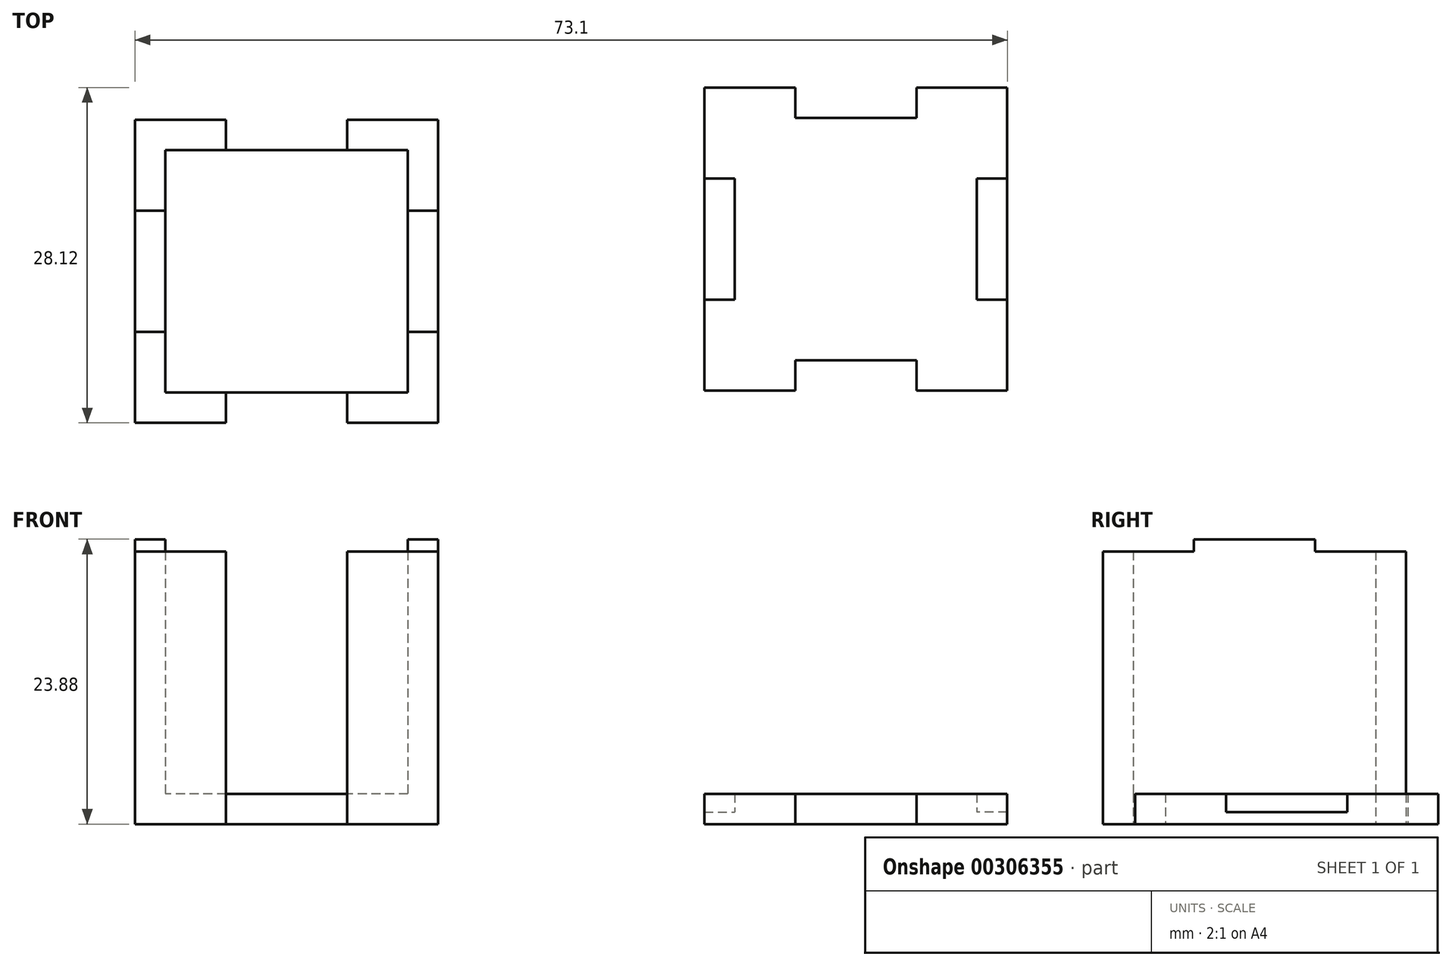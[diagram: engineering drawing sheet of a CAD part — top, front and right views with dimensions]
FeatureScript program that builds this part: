
annotation { "Feature Type Name" : "Feature", "Feature Type Description" : "" }
export const myFeature = defineFeature(function(context is Context, id is Id, definition is map)
    precondition{}
    {
        {
            var Q0;
            Q0=qCreatedBy(makeId("Top.planeOp"),FACE);
            var sketch = newSketch(context, id + "F0", { "sketchPlane" : qUnion([Q0])});
            skLineSegment(sketch, "E0.bottom", {"start": v(12.7, -12.7) * mm, "end": v(-12.7, -12.7) * mm});
            skLineSegment(sketch, "E0.top", {"start": v(12.7, 12.7) * mm, "end": v(-12.7, 12.7) * mm});
            skLineSegment(sketch, "E0.left", {"start": v(12.7, -12.7) * mm, "end": v(12.7, 12.7) * mm});
            skLineSegment(sketch, "E0.right", {"start": v(-12.7, -12.7) * mm, "end": v(-12.7, 12.7) * mm});
            skPoint(sketch, "E0.middle", {"position": v(0, 0) * mm});
            skLineSegment(sketch, "E1.bottom", {"start": v(-5.08, 12.7) * mm, "end": v(5.08, 12.7) * mm});
            skLineSegment(sketch, "E1.top", {"start": v(-5.08, 10.16) * mm, "end": v(5.08, 10.16) * mm});
            skLineSegment(sketch, "E1.left", {"start": v(-5.08, 12.7) * mm, "end": v(-5.08, 10.16) * mm});
            skLineSegment(sketch, "E1.right", {"start": v(5.08, 12.7) * mm, "end": v(5.08, 10.16) * mm});
            skLineSegment(sketch, "E2.bottom", {"start": v(-12.7, 5.08) * mm, "end": v(-10.16, 5.08) * mm});
            skLineSegment(sketch, "E2.top", {"start": v(-12.7, -5.08) * mm, "end": v(-10.16, -5.08) * mm});
            skLineSegment(sketch, "E2.left", {"start": v(-12.7, 5.08) * mm, "end": v(-12.7, -5.08) * mm});
            skLineSegment(sketch, "E2.right", {"start": v(-10.16, 5.08) * mm, "end": v(-10.16, -5.08) * mm});
            skLineSegment(sketch, "E3.bottom", {"start": v(-5.08, -12.7) * mm, "end": v(5.08, -12.7) * mm});
            skLineSegment(sketch, "E3.top", {"start": v(-5.08, -10.16) * mm, "end": v(5.08, -10.16) * mm});
            skLineSegment(sketch, "E3.left", {"start": v(-5.08, -12.7) * mm, "end": v(-5.08, -10.16) * mm});
            skLineSegment(sketch, "E3.right", {"start": v(5.08, -12.7) * mm, "end": v(5.08, -10.16) * mm});
            skLineSegment(sketch, "E4.bottom", {"start": v(12.7, 5.08) * mm, "end": v(10.16, 5.08) * mm});
            skLineSegment(sketch, "E4.top", {"start": v(12.7, -5.08) * mm, "end": v(10.16, -5.08) * mm});
            skLineSegment(sketch, "E4.left", {"start": v(12.7, 5.08) * mm, "end": v(12.7, -5.08) * mm});
            skLineSegment(sketch, "E4.right", {"start": v(10.16, 5.08) * mm, "end": v(10.16, -5.08) * mm});
            skLineSegment(sketch, "E5.bottom", {"start": v(10.16, -10.16) * mm, "end": v(-10.16, -10.16) * mm});
            skLineSegment(sketch, "E5.top", {"start": v(10.16, 10.16) * mm, "end": v(-10.16, 10.16) * mm});
            skLineSegment(sketch, "E5.left", {"start": v(10.16, -10.16) * mm, "end": v(10.16, 10.16) * mm});
            skLineSegment(sketch, "E5.right", {"start": v(-10.16, -10.16) * mm, "end": v(-10.16, 10.16) * mm});
            skLineSegment(sketch, "E6.bottom", {"start": v(60.4, -9.98) * mm, "end": v(35, -9.98) * mm});
            skLineSegment(sketch, "E6.top", {"start": v(60.4, 15.42) * mm, "end": v(35, 15.42) * mm});
            skLineSegment(sketch, "E6.left", {"start": v(60.4, -9.98) * mm, "end": v(60.4, 15.42) * mm});
            skLineSegment(sketch, "E6.right", {"start": v(35, -9.98) * mm, "end": v(35, 15.42) * mm});
            skPoint(sketch, "E6.middle", {"position": v(47.7, 2.72) * mm});
            skLineSegment(sketch, "E7.bottom", {"start": v(42.62, 15.42) * mm, "end": v(52.78, 15.42) * mm});
            skLineSegment(sketch, "E7.top", {"start": v(42.62, 12.88) * mm, "end": v(52.78, 12.88) * mm});
            skLineSegment(sketch, "E7.left", {"start": v(42.62, 15.42) * mm, "end": v(42.62, 12.88) * mm});
            skLineSegment(sketch, "E7.right", {"start": v(52.78, 15.42) * mm, "end": v(52.78, 12.88) * mm});
            skLineSegment(sketch, "E8.bottom", {"start": v(35, 7.8) * mm, "end": v(37.54, 7.8) * mm});
            skLineSegment(sketch, "E8.top", {"start": v(35, -2.36) * mm, "end": v(37.54, -2.36) * mm});
            skLineSegment(sketch, "E8.left", {"start": v(35, 7.8) * mm, "end": v(35, -2.36) * mm});
            skLineSegment(sketch, "E8.right", {"start": v(37.54, 7.8) * mm, "end": v(37.54, -2.36) * mm});
            skLineSegment(sketch, "E9.bottom", {"start": v(42.62, -9.98) * mm, "end": v(52.78, -9.98) * mm});
            skLineSegment(sketch, "E9.top", {"start": v(42.62, -7.44) * mm, "end": v(52.78, -7.44) * mm});
            skLineSegment(sketch, "E9.left", {"start": v(42.62, -9.98) * mm, "end": v(42.62, -7.44) * mm});
            skLineSegment(sketch, "E9.right", {"start": v(52.78, -9.98) * mm, "end": v(52.78, -7.44) * mm});
            skLineSegment(sketch, "E10.bottom", {"start": v(60.4, 7.8) * mm, "end": v(57.86, 7.8) * mm});
            skLineSegment(sketch, "E10.top", {"start": v(60.4, -2.36) * mm, "end": v(57.86, -2.36) * mm});
            skLineSegment(sketch, "E10.left", {"start": v(60.4, 7.8) * mm, "end": v(60.4, -2.36) * mm});
            skLineSegment(sketch, "E10.right", {"start": v(57.86, 7.8) * mm, "end": v(57.86, -2.36) * mm});
            skLineSegment(sketch, "E11.bottom", {"start": v(57.86, -7.44) * mm, "end": v(37.54, -7.44) * mm});
            skLineSegment(sketch, "E11.top", {"start": v(57.86, 12.88) * mm, "end": v(37.54, 12.88) * mm});
            skLineSegment(sketch, "E11.left", {"start": v(57.86, -7.44) * mm, "end": v(57.86, 12.88) * mm});
            skLineSegment(sketch, "E11.right", {"start": v(37.54, -7.44) * mm, "end": v(37.54, 12.88) * mm});
            skSolve(sketch);
        }
        {
            var Q0;
            {var subQ2=sQuery(id+"F0.wireOp",EDGE,"E5.bottom");var subQ13=makeQuery(id+"F0.imprint","INTERSECT",VERTEX,{"derivedFrom":[sQuery(id+"F0.wireOp",EDGE,"E3.right"),subQ2]});Q0=makeQuery(id+"F0.imprint","IMPRINT",FACE,{"disambiguationData":[TD([[makeQuery(id+"F0.imprint","IMPRINT",EDGE,{"disambiguationData":[TD([[subQ13,1.0]])],"derivedFrom":subQ2}),-1.0]])]});}
            var Q1;
            {var subQ2=sQuery(id+"F0.wireOp",EDGE,"E11.bottom");var subQ13=makeQuery(id+"F0.imprint","INTERSECT",VERTEX,{"derivedFrom":[sQuery(id+"F0.wireOp",EDGE,"E9.right"),subQ2]});Q1=makeQuery(id+"F0.imprint","IMPRINT",FACE,{"disambiguationData":[TD([[makeQuery(id+"F0.imprint","IMPRINT",EDGE,{"disambiguationData":[TD([[subQ13,1.0]])],"derivedFrom":subQ2}),-1.0]])]});}
            var Q2;
            {var subQ1=sQuery(id+"F0.wireOp",EDGE,"E7.left");Q2=makeQuery(id+"F0.imprint","IMPRINT",FACE,{"disambiguationData":[TD([[makeQuery(id+"F0.imprint","IMPRINT",EDGE,{"derivedFrom":subQ1}),-1.0]])]});}
            var Q3;
            {var subQ0=sQuery(id+"F0.wireOp",EDGE,"E7.right");Q3=makeQuery(id+"F0.imprint","IMPRINT",FACE,{"disambiguationData":[TD([[makeQuery(id+"F0.imprint","IMPRINT",EDGE,{"derivedFrom":subQ0}),1.0]])]});}
            var Q4;
            {var subQ1=sQuery(id+"F0.wireOp",EDGE,"E9.right");Q4=makeQuery(id+"F0.imprint","IMPRINT",FACE,{"disambiguationData":[TD([[makeQuery(id+"F0.imprint","IMPRINT",EDGE,{"derivedFrom":subQ1}),-1.0]])]});}
            var Q5;
            {var subQ1=sQuery(id+"F0.wireOp",EDGE,"E8.top");Q5=makeQuery(id+"F0.imprint","IMPRINT",FACE,{"disambiguationData":[TD([[makeQuery(id+"F0.imprint","IMPRINT",EDGE,{"derivedFrom":subQ1}),-1.0]])]});}
            extrude(context, id + "F1", {"entities" : qUnion([Q0, Q1, Q2, Q3, Q4, Q5]), "depth" : 2.54 * mm});
        }
        {
            var Q0;
            Q0=makeQuery(id+"F0.imprint","IMPRINT",FACE,{"disambiguationData":[TD([[makeQuery(id+"F0.imprint","IMPRINT",EDGE,{"derivedFrom":sQuery(id+"F0.wireOp",EDGE,"E1.bottom")}),-1.0]])]});
            var Q1;
            {var subQ0=sQuery(id+"F0.wireOp",EDGE,"E4.bottom");Q1=makeQuery(id+"F0.imprint","IMPRINT",FACE,{"disambiguationData":[TD([[makeQuery(id+"F0.imprint","IMPRINT",EDGE,{"derivedFrom":subQ0}),1.0]])]});}
            var Q2;
            Q2=makeQuery(id+"F0.imprint","IMPRINT",FACE,{"disambiguationData":[TD([[makeQuery(id+"F0.imprint","IMPRINT",EDGE,{"derivedFrom":sQuery(id+"F0.wireOp",EDGE,"E3.bottom")}),1.0]])]});
            var Q3;
            {var subQ0=sQuery(id+"F0.wireOp",EDGE,"E2.bottom");Q3=makeQuery(id+"F0.imprint","IMPRINT",FACE,{"disambiguationData":[TD([[makeQuery(id+"F0.imprint","IMPRINT",EDGE,{"derivedFrom":subQ0}),-1.0]])]});}
            extrude(context, id + "F2", {"entities" : qUnion([Q0, Q1, Q2, Q3]), "operationType" : NewBodyOperationType.ADD, "depth" : 23.88 * mm});
        }
        {
            var Q0;
            {var subQ1=sQuery(id+"F0.wireOp",EDGE,"E1.left");Q0=makeQuery(id+"F0.imprint","IMPRINT",FACE,{"disambiguationData":[TD([[makeQuery(id+"F0.imprint","IMPRINT",EDGE,{"derivedFrom":subQ1}),-1.0]])]});}
            var Q1;
            {var subQ0=sQuery(id+"F0.wireOp",EDGE,"E1.right");Q1=makeQuery(id+"F0.imprint","IMPRINT",FACE,{"disambiguationData":[TD([[makeQuery(id+"F0.imprint","IMPRINT",EDGE,{"derivedFrom":subQ0}),1.0]])]});}
            var Q2;
            {var subQ1=sQuery(id+"F0.wireOp",EDGE,"E2.top");Q2=makeQuery(id+"F0.imprint","IMPRINT",FACE,{"disambiguationData":[TD([[makeQuery(id+"F0.imprint","IMPRINT",EDGE,{"derivedFrom":subQ1}),-1.0]])]});}
            var Q3;
            {var subQ1=sQuery(id+"F0.wireOp",EDGE,"E3.right");Q3=makeQuery(id+"F0.imprint","IMPRINT",FACE,{"disambiguationData":[TD([[makeQuery(id+"F0.imprint","IMPRINT",EDGE,{"derivedFrom":subQ1}),-1.0]])]});}
            extrude(context, id + "F3", {"entities" : qUnion([Q0, Q1, Q2, Q3]), "operationType" : NewBodyOperationType.ADD, "depth" : 22.86 * mm});
        }
        {
            var Q0;
            {var subQ0=sQuery(id+"F0.wireOp",EDGE,"E8.bottom");Q0=makeQuery(id+"F0.imprint","IMPRINT",FACE,{"disambiguationData":[TD([[makeQuery(id+"F0.imprint","IMPRINT",EDGE,{"derivedFrom":subQ0}),-1.0]])]});}
            var Q1;
            Q1=makeQuery(id+"F0.imprint","IMPRINT",FACE,{"disambiguationData":[TD([[makeQuery(id+"F0.imprint","IMPRINT",EDGE,{"derivedFrom":sQuery(id+"F0.wireOp",EDGE,"E7.bottom")}),-1.0]])]});
            var Q2;
            {var subQ0=sQuery(id+"F0.wireOp",EDGE,"E10.bottom");Q2=makeQuery(id+"F0.imprint","IMPRINT",FACE,{"disambiguationData":[TD([[makeQuery(id+"F0.imprint","IMPRINT",EDGE,{"derivedFrom":subQ0}),1.0]])]});}
            var Q3;
            Q3=makeQuery(id+"F0.imprint","IMPRINT",FACE,{"disambiguationData":[TD([[makeQuery(id+"F0.imprint","IMPRINT",EDGE,{"derivedFrom":sQuery(id+"F0.wireOp",EDGE,"E9.bottom")}),1.0]])]});
            extrude(context, id + "F4", {"entities" : qUnion([Q0, Q1, Q2, Q3]), "operationType" : NewBodyOperationType.ADD, "depth" : 1.02 * mm});
        }
    });
